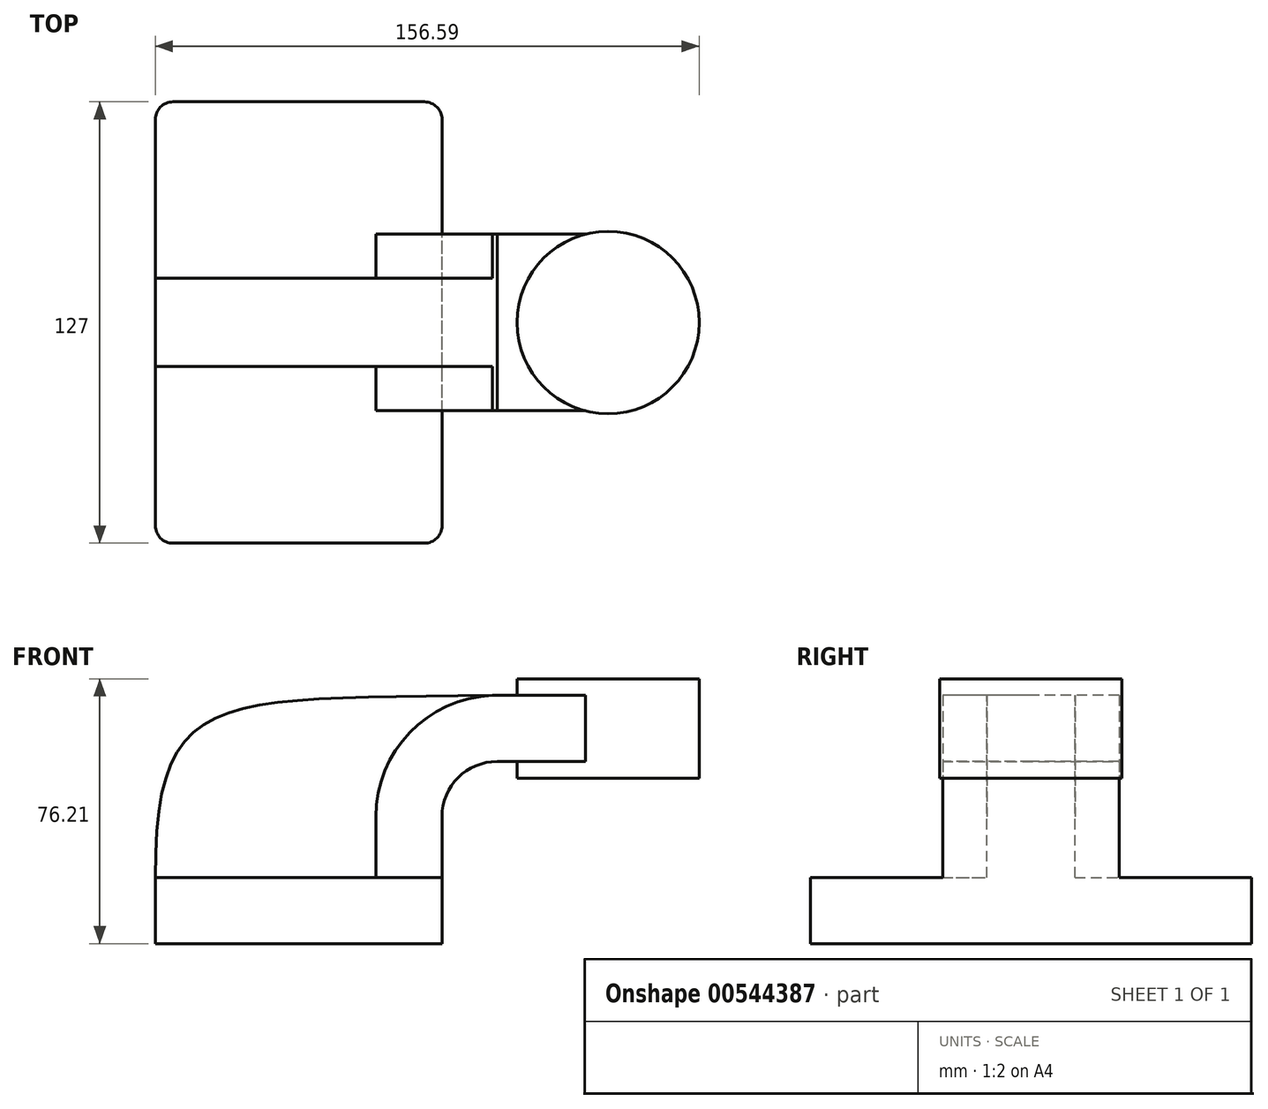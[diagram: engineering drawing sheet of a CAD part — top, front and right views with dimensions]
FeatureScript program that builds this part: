
annotation { "Feature Type Name" : "Feature", "Feature Type Description" : "" }
export const myFeature = defineFeature(function(context is Context, id is Id, definition is map)
    precondition{}
    {
        {
            var Q0;
            Q0=qCreatedBy(makeId("Front.planeOp"),FACE);
            var sketch = newSketch(context, id + "F0", { "sketchPlane" : qUnion([Q0])});
            skLineSegment(sketch, "E0.bottom", {"start": v(-41.27, -9.52) * mm, "end": v(41.28, -9.52) * mm});
            skLineSegment(sketch, "E0.top", {"start": v(-41.28, 9.53) * mm, "end": v(41.27, 9.53) * mm});
            skLineSegment(sketch, "E0.left", {"start": v(-41.27, -9.52) * mm, "end": v(-41.28, 9.53) * mm});
            skLineSegment(sketch, "E0.right", {"start": v(41.28, -9.53) * mm, "end": v(41.27, 9.53) * mm});
            skPoint(sketch, "E0.middle", {"position": v(0, 0) * mm});
            skPoint(sketch, "E1.middle", {"position": v(78.38, 90.7) * mm});
            skLineSegment(sketch, "E2.bottom", {"start": v(115.31, 38.1) * mm, "end": v(64.51, 38.1) * mm});
            skLineSegment(sketch, "E2.top", {"start": v(115.31, 66.68) * mm, "end": v(64.51, 66.68) * mm});
            skLineSegment(sketch, "E2.left", {"start": v(115.31, 38.1) * mm, "end": v(115.31, 66.68) * mm});
            skLineSegment(sketch, "E2.right", {"start": v(64.51, 38.1) * mm, "end": v(64.51, 66.68) * mm});
            skPoint(sketch, "E2.middle", {"position": v(89.91, 52.39) * mm});
            skLineSegment(sketch, "E3.left", {"start": v(89.91, 52.39) * mm, "end": v(89.91, 52.39) * mm});
            skPoint(sketch, "E3.middle", {"position": v(64.51, 52.39) * mm});
            skLineSegment(sketch, "E4", {"start": v(41.27, 9.53) * mm, "end": v(41.27, 27) * mm});
            skArc(sketch, "E5", {"start": v(41.27, 27) * mm, "mid": v(45.92, 38.23) * mm, "end": v(57.15, 42.88) * mm});
            skLineSegment(sketch, "E6", {"start": v(57.15, 42.88) * mm, "end": v(89.1, 42.88) * mm});
            skLineSegment(sketch, "E7.0", {"start": v(57.15, 61.93) * mm, "end": v(89.1, 61.93) * mm});
            skArc(sketch, "E7.1", {"start": v(22.22, 27) * mm, "mid": v(32.45, 51.7) * mm, "end": v(57.15, 61.93) * mm});
            skLineSegment(sketch, "E7.2", {"start": v(22.22, 9.53) * mm, "end": v(22.22, 27) * mm});
            skLineSegment(sketch, "E8", {"start": v(89.1, 38.1) * mm, "end": v(89.1, 66.68) * mm});
            skFitSpline(sketch, "E9", {"points": [v(-41.28, 9.53) * mm, v(57.15, 61.93) * mm], "startDerivative": vector(-0.52, 168.94) * mm, "endDerivative": vector(238.34, 4.78) * mm});
            skSolve(sketch);
        }
        {
            var Q0;
            Q0=makeQuery(id+"F0.imprint","IMPRINT",FACE,{"disambiguationData":[TD([[makeQuery(id+"F0.imprint","IMPRINT",EDGE,{"derivedFrom":sQuery(id+"F0.wireOp",EDGE,"E0.bottom")}),1.0]])]});
            extrude(context, id + "F1", {"entities" : qUnion([Q0]), "endBound" : BoundingType.SYMMETRIC, "depth" : 127 * mm, "offsetDistance" : 25.4 * mm});
        }
        {
            var Q0;
            {var subQ1=sQuery(id+"F0.wireOp",EDGE,"E4");Q0=makeQuery(id+"F0.imprint","IMPRINT",FACE,{"disambiguationData":[TD([[makeQuery(id+"F0.imprint","IMPRINT",EDGE,{"derivedFrom":subQ1}),1.0]])]});}
            var Q1;
            {var subQ0=sQuery(id+"F0.wireOp",EDGE,"E6");var subQ1=sQuery(id+"F0.wireOp",EDGE,"E2.right");var subQ2=makeQuery(id+"F0.imprint","INTERSECT",VERTEX,{"derivedFrom":[subQ1,subQ0]});Q1=makeQuery(id+"F0.imprint","IMPRINT",FACE,{"disambiguationData":[TD([[makeQuery(id+"F0.imprint","IMPRINT",EDGE,{"disambiguationData":[TD([[subQ2,-1.0]])],"derivedFrom":subQ1}),-1.0]])]});}
            extrude(context, id + "F2", {"entities" : qUnion([Q0, Q1]), "operationType" : NewBodyOperationType.ADD, "endBound" : BoundingType.SYMMETRIC, "depth" : 50.8 * mm, "offsetDistance" : 25.4 * mm});
        }
        {
            var Q0;
            {var subQ3=sQuery(id+"F0.wireOp",EDGE,"E7.2");Q0=makeQuery(id+"F0.imprint","IMPRINT",FACE,{"disambiguationData":[TD([[makeQuery(id+"F0.imprint","IMPRINT",EDGE,{"derivedFrom":subQ3}),1.0]])]});}
            extrude(context, id + "F3", {"entities" : qUnion([Q0]), "operationType" : NewBodyOperationType.ADD, "endBound" : BoundingType.SYMMETRIC, "depth" : 25.4 * mm, "offsetDistance" : 25.4 * mm});
        }
        {
            var Q0;
            {var subQ0=sQuery(id+"F0.wireOp",EDGE,"E2.left");Q0=makeQuery(id+"F0.imprint","IMPRINT",FACE,{"disambiguationData":[TD([[makeQuery(id+"F0.imprint","IMPRINT",EDGE,{"derivedFrom":subQ0}),1.0]])]});}
            var Q1;
            Q1=sQuery(id+"F0.wireOp",EDGE,"E8");
            revolve(context, id + "F4", {"operationType" : NewBodyOperationType.ADD, "entities" : qUnion([Q0]), "axis" : qUnion([Q1]), "revolveType" : RevolveType.FULL});
        }
        {
            var Q0;
            Q0=makeQuery(id+"F1.opExtrude","CAP_EDGE",EDGE,{"disambiguationData":[OSD([sQuery(id+"F0.wireOp",EDGE,"E0.right")])],"isStart":false});
            var Q1;
            Q1=makeQuery(id+"F1.opExtrude","CAP_EDGE",EDGE,{"disambiguationData":[OSD([sQuery(id+"F0.wireOp",EDGE,"E0.left")])],"isStart":false});
            var Q2;
            Q2=makeQuery(id+"F1.opExtrude","CAP_EDGE",EDGE,{"disambiguationData":[OSD([sQuery(id+"F0.wireOp",EDGE,"E0.right")])],"isStart":true});
            var Q3;
            Q3=makeQuery(id+"F1.opExtrude","CAP_EDGE",EDGE,{"disambiguationData":[OSD([sQuery(id+"F0.wireOp",EDGE,"E0.left")])],"isStart":true});
            fillet(context, id + "F5", {"entities" : qUnion([Q0, Q1, Q2, Q3]), "radius" : 5.08 * mm, "tangentPropagation" : true, "allowEdgeOverflow" : false});
        }
    });
